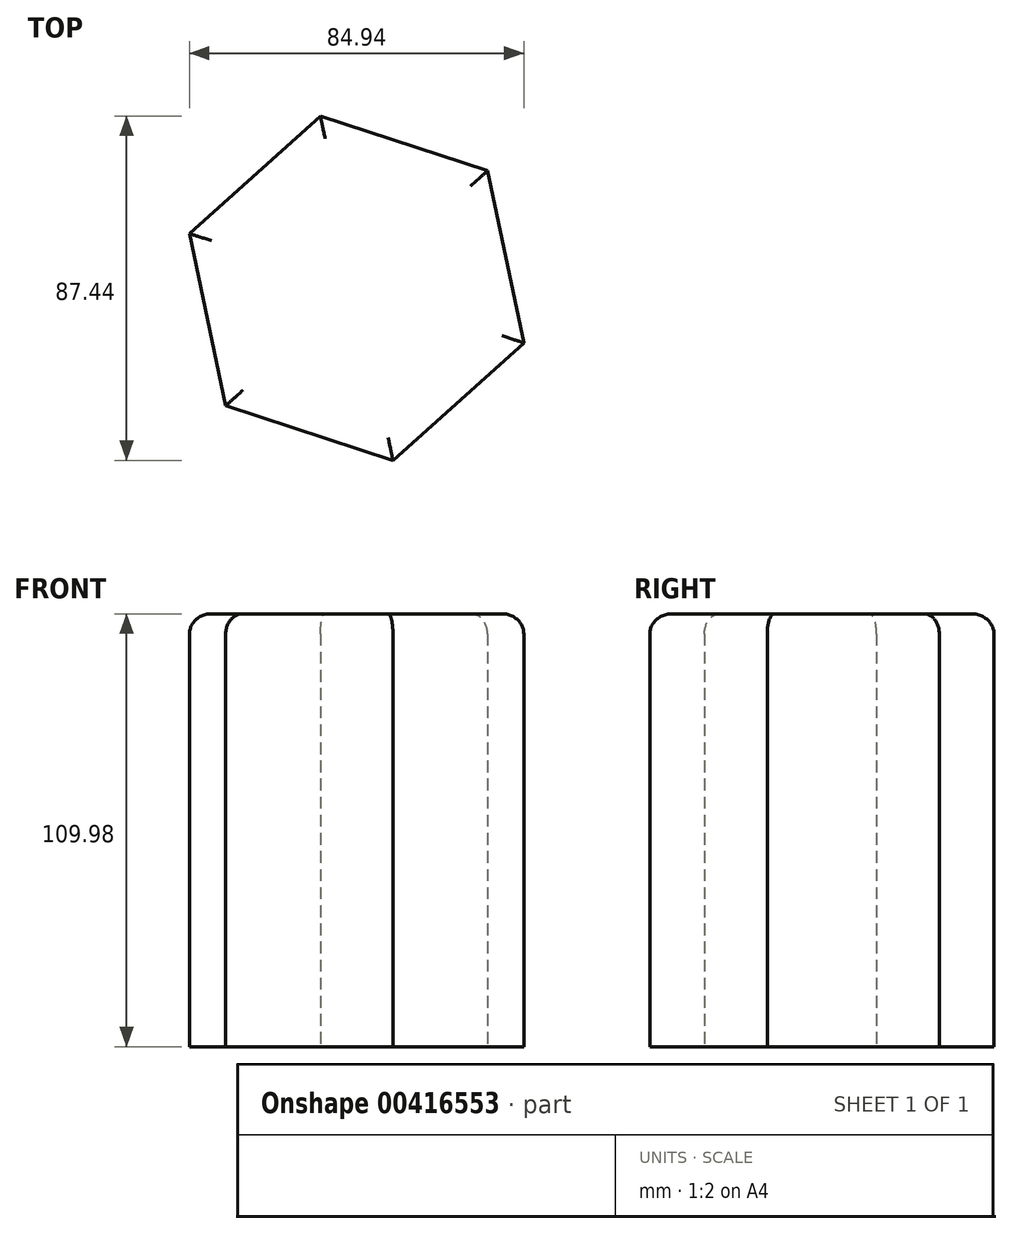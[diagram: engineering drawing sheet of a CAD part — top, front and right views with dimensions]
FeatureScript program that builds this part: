
annotation { "Feature Type Name" : "Feature", "Feature Type Description" : "" }
export const myFeature = defineFeature(function(context is Context, id is Id, definition is map)
    precondition{}
    {
        {
            var Q0;
            Q0=qCreatedBy(makeId("Top.planeOp"),FACE);
            var sketch = newSketch(context, id + "F0", { "sketchPlane" : qUnion([Q0])});
            skCircle(sketch, "E0.cCircle", {"center": v(0, 0) * mm, "radius": 44.68 * mm, "construction": true});
            skLineSegment(sketch, "E0.0", {"start": v(42.47, -13.89) * mm, "end": v(9.2, -43.72) * mm});
            skLineSegment(sketch, "E0.1", {"start": v(9.2, -43.72) * mm, "end": v(-33.26, -29.83) * mm});
            skLineSegment(sketch, "E0.2", {"start": v(-33.26, -29.83) * mm, "end": v(-42.47, 13.89) * mm});
            skLineSegment(sketch, "E0.3", {"start": v(-42.47, 13.89) * mm, "end": v(-9.2, 43.72) * mm});
            skLineSegment(sketch, "E0.4", {"start": v(-9.2, 43.72) * mm, "end": v(33.26, 29.83) * mm});
            skLineSegment(sketch, "E0.5", {"start": v(33.26, 29.83) * mm, "end": v(42.47, -13.89) * mm});
            skSolve(sketch);
        }
        {
            var Q0;
            Q0=makeQuery(id+"F0.imprint","IMPRINT",FACE,{"disambiguationData":[TD([[makeQuery(id+"F0.imprint","IMPRINT",EDGE,{"derivedFrom":sQuery(id+"F0.wireOp",EDGE,"E0.0")}),-1.0]])]});
            extrude(context, id + "F1", {"entities" : qUnion([Q0]), "depth" : 109.98 * mm});
        }
        {
            var Q0;
            Q0=makeQuery(id+"F1.opExtrude","CAP_FACE",FACE,{"disambiguationData":[OSD([sQuery(id+"F0.wireOp",EDGE,"E0.0"),sQuery(id+"F0.wireOp",EDGE,"E0.1"),sQuery(id+"F0.wireOp",EDGE,"E0.2"),sQuery(id+"F0.wireOp",EDGE,"E0.3"),sQuery(id+"F0.wireOp",EDGE,"E0.4"),sQuery(id+"F0.wireOp",EDGE,"E0.5")])],"isStart":false});
            fillet(context, id + "F2", {"entities" : qUnion([Q0]), "radius" : 5.08 * mm, "tangentPropagation" : true, "allowEdgeOverflow" : false});
        }
    });
